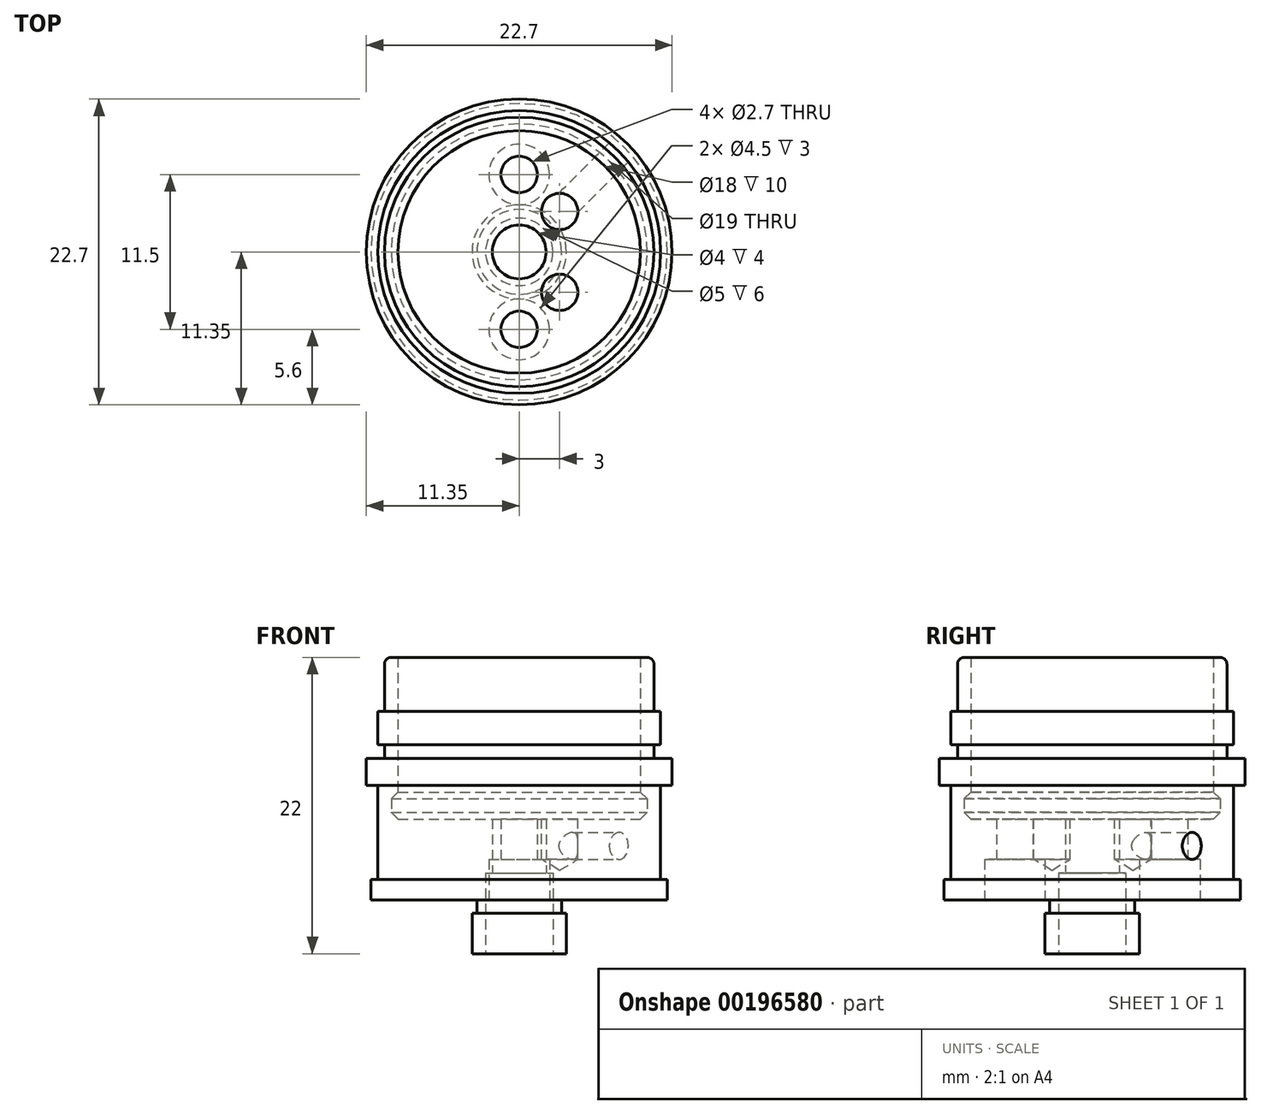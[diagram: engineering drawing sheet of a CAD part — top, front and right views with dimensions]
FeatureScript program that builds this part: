
annotation { "Feature Type Name" : "Feature", "Feature Type Description" : "" }
export const myFeature = defineFeature(function(context is Context, id is Id, definition is map)
    precondition{}
    {
        {
            var Q0;
            Q0=qCreatedBy(makeId("Front.planeOp"),FACE);
            var sketch = newSketch(context, id + "F0", { "sketchPlane" : qUnion([Q0])});
            skLineSegment(sketch, "E0", {"start": v(0, 0) * mm, "end": v(0, 22) * mm, "construction": true});
            skLineSegment(sketch, "E1", {"start": v(9, 22) * mm, "end": v(9.5, 22) * mm});
            skLineSegment(sketch, "E2", {"start": v(10, 21.5) * mm, "end": v(10, 18) * mm});
            skLineSegment(sketch, "E3", {"start": v(10, 18) * mm, "end": v(10.5, 18) * mm});
            skLineSegment(sketch, "E4", {"start": v(10.5, 18) * mm, "end": v(10.5, 15.5) * mm});
            skLineSegment(sketch, "E5", {"start": v(10.5, 15.5) * mm, "end": v(10, 15.5) * mm});
            skLineSegment(sketch, "E6", {"start": v(10, 15.5) * mm, "end": v(10, 14.5) * mm});
            skLineSegment(sketch, "E7", {"start": v(10, 14.5) * mm, "end": v(11.35, 14.5) * mm});
            skLineSegment(sketch, "E8", {"start": v(11.35, 14.5) * mm, "end": v(11.35, 12.5) * mm});
            skLineSegment(sketch, "E9", {"start": v(11.35, 12.5) * mm, "end": v(10.5, 12.5) * mm});
            skLineSegment(sketch, "E10", {"start": v(10.5, 12.5) * mm, "end": v(10.5, 5.5) * mm});
            skLineSegment(sketch, "E11", {"start": v(10.5, 5.5) * mm, "end": v(11, 5.5) * mm});
            skLineSegment(sketch, "E12", {"start": v(9, 22) * mm, "end": v(9, 12) * mm});
            skLineSegment(sketch, "E13", {"start": v(0, 4.88) * mm, "end": v(0, 0) * mm, "construction": true});
            skLineSegment(sketch, "E14", {"start": v(11, 5.5) * mm, "end": v(11, 4) * mm});
            skLineSegment(sketch, "E15", {"start": v(11, 4) * mm, "end": v(3.15, 4) * mm});
            skLineSegment(sketch, "E16", {"start": v(3.15, 4) * mm, "end": v(3.15, 3) * mm});
            skLineSegment(sketch, "E17", {"start": v(3.15, 3) * mm, "end": v(3.5, 3) * mm});
            skLineSegment(sketch, "E18", {"start": v(3.5, 3) * mm, "end": v(3.5, 0) * mm});
            skLineSegment(sketch, "E19", {"start": v(3.5, 0) * mm, "end": v(2.5, 0) * mm});
            skLineSegment(sketch, "E20", {"start": v(2.5, 0) * mm, "end": v(2.5, 6) * mm});
            skLineSegment(sketch, "E21", {"start": v(2.5, 6) * mm, "end": v(2, 6) * mm});
            skLineSegment(sketch, "E22", {"start": v(2, 6) * mm, "end": v(2, 10) * mm});
            skLineSegment(sketch, "E23", {"start": v(9, 10) * mm, "end": v(2, 10) * mm});
            skPoint(sketch, "E24.visualSharp", {"position": v(10, 22) * mm});
            skArc(sketch, "E24.filletArc", {"start": v(10, 21.5) * mm, "mid": v(9.85, 21.85) * mm, "end": v(9.5, 22) * mm});
            skLineSegment(sketch, "E25", {"start": v(9, 12) * mm, "end": v(9.5, 11.5) * mm});
            skLineSegment(sketch, "E26", {"start": v(9.5, 11.5) * mm, "end": v(9.5, 10.5) * mm});
            skLineSegment(sketch, "E27", {"start": v(9, 10) * mm, "end": v(9.5, 10.5) * mm});
            skSolve(sketch);
        }
        {
            var Q0;
            Q0 = qSketchRegion(id + "F0", true);
            var Q1;
            Q1=sQuery(id+"F0.wireOp",EDGE,"E0");
            revolve(context, id + "F1", {"entities" : qUnion([Q0]), "axis" : qUnion([Q1]), "revolveType" : RevolveType.FULL});
        }
        {
            var Q0;
            Q0=makeQuery(id+"F1.opRevolve","SWEPT_FACE",FACE,{"disambiguationData":[OSD([sQuery(id+"F0.wireOp",EDGE,"E15")])]});
            var sketch = newSketch(context, id + "F2", { "sketchPlane" : qUnion([Q0])});
            skPoint(sketch, "E28", {"position": v(0, -5.75) * mm});
            skPoint(sketch, "E29.MirrorP", {"position": v(0, 5.75) * mm});
            skSolve(sketch);
        }
        {
            var Q0;
            Q0=sQuery(id+"F2.wireOp",VERTEX,"E28");
            var Q1;
            Q1=sQuery(id+"F2.wireOp",VERTEX,"E29.MirrorP");
            var Q2;
            Q2=makeQuery(id+"F1.opRevolve","SWEPT_BODY",BODY,{"disambiguationData":[OSD([sQuery(id+"F0.wireOp",EDGE,"E1"),sQuery(id+"F0.wireOp",EDGE,"E2"),sQuery(id+"F0.wireOp",EDGE,"E3"),sQuery(id+"F0.wireOp",EDGE,"E4"),sQuery(id+"F0.wireOp",EDGE,"E5"),sQuery(id+"F0.wireOp",EDGE,"E6"),sQuery(id+"F0.wireOp",EDGE,"E7"),sQuery(id+"F0.wireOp",EDGE,"E8"),sQuery(id+"F0.wireOp",EDGE,"E9"),sQuery(id+"F0.wireOp",EDGE,"E10"),sQuery(id+"F0.wireOp",EDGE,"E11"),sQuery(id+"F0.wireOp",EDGE,"E12"),sQuery(id+"F0.wireOp",EDGE,"E14"),sQuery(id+"F0.wireOp",EDGE,"E15"),sQuery(id+"F0.wireOp",EDGE,"E16"),sQuery(id+"F0.wireOp",EDGE,"E17"),sQuery(id+"F0.wireOp",EDGE,"E18"),sQuery(id+"F0.wireOp",EDGE,"E19"),sQuery(id+"F0.wireOp",EDGE,"E20"),sQuery(id+"F0.wireOp",EDGE,"E21"),sQuery(id+"F0.wireOp",EDGE,"E22"),sQuery(id+"F0.wireOp",EDGE,"E23"),sQuery(id+"F0.wireOp",EDGE,"E24.filletArc"),sQuery(id+"F0.wireOp",EDGE,"E25"),sQuery(id+"F0.wireOp",EDGE,"E26"),sQuery(id+"F0.wireOp",EDGE,"E27")])]});
            hole(context, id + "F3", {"style" : HoleStyle.C_BORE, "endStyle" : HoleEndStyle.THROUGH, "holeDiameter" : 2.7 * mm, "cBoreDiameter" : 4.5 * mm, "cBoreDepth" : 3 * mm, "locations" : qUnion([Q0, Q1]), "scope" : qUnion([Q2]), "isTappedThrough" : true});
        }
        {
            var Q0;
            Q0=makeQuery(id+"F1.opRevolve","SWEPT_FACE",FACE,{"disambiguationData":[OSD([sQuery(id+"F0.wireOp",EDGE,"E23")])]});
            var sketch = newSketch(context, id + "F4", { "sketchPlane" : qUnion([Q0])});
            skPoint(sketch, "E30", {"position": v(3, -3) * mm});
            skPoint(sketch, "E31.MirrorP", {"position": v(3, 3) * mm});
            skSolve(sketch);
        }
        {
            var Q0;
            Q0=sQuery(id+"F4.wireOp",VERTEX,"E30");
            var Q1;
            Q1=sQuery(id+"F4.wireOp",VERTEX,"E31.MirrorP");
            var Q2;
            Q2=makeQuery(id+"F1.opRevolve","SWEPT_BODY",BODY,{"disambiguationData":[OSD([sQuery(id+"F0.wireOp",EDGE,"E1"),sQuery(id+"F0.wireOp",EDGE,"E2"),sQuery(id+"F0.wireOp",EDGE,"E3"),sQuery(id+"F0.wireOp",EDGE,"E4"),sQuery(id+"F0.wireOp",EDGE,"E5"),sQuery(id+"F0.wireOp",EDGE,"E6"),sQuery(id+"F0.wireOp",EDGE,"E7"),sQuery(id+"F0.wireOp",EDGE,"E8"),sQuery(id+"F0.wireOp",EDGE,"E9"),sQuery(id+"F0.wireOp",EDGE,"E10"),sQuery(id+"F0.wireOp",EDGE,"E11"),sQuery(id+"F0.wireOp",EDGE,"E12"),sQuery(id+"F0.wireOp",EDGE,"E14"),sQuery(id+"F0.wireOp",EDGE,"E15"),sQuery(id+"F0.wireOp",EDGE,"E16"),sQuery(id+"F0.wireOp",EDGE,"E17"),sQuery(id+"F0.wireOp",EDGE,"E18"),sQuery(id+"F0.wireOp",EDGE,"E19"),sQuery(id+"F0.wireOp",EDGE,"E20"),sQuery(id+"F0.wireOp",EDGE,"E21"),sQuery(id+"F0.wireOp",EDGE,"E22"),sQuery(id+"F0.wireOp",EDGE,"E23"),sQuery(id+"F0.wireOp",EDGE,"E24.filletArc"),sQuery(id+"F0.wireOp",EDGE,"E25"),sQuery(id+"F0.wireOp",EDGE,"E26"),sQuery(id+"F0.wireOp",EDGE,"E27")])]});
            hole(context, id + "F5", {"style" : HoleStyle.SIMPLE, "endStyle" : HoleEndStyle.BLIND, "holeDiameter" : 2.7 * mm, "holeDepth" : 3 * mm, "locations" : qUnion([Q0, Q1]), "scope" : qUnion([Q2])});
        }
        {
            var Q0;
            Q0=sQuery(id+"F0.wireOp",EDGE,"E0");
            var Q1;
            Q1=sQuery(id+"F4.wireOp",VERTEX,"E31.MirrorP");
            cPlane(context, id + "F6", {"entities" : qUnion([Q0, Q1]), "cplaneType" : CPlaneType.LINE_ANGLE, "offset" : 25 * mm, "angle" : 0 * degree, "width" : 150 * mm, "height" : 150 * mm});
        }
        {
            var Q0;
            Q0=qCreatedBy(id+"F6.planeOp",FACE);
            var sketch = newSketch(context, id + "F7", { "sketchPlane" : qUnion([Q0])});
            skLineSegment(sketch, "E32", {"start": v(-4.24, 8) * mm, "end": v(-16.96, 8) * mm});
            skLineSegment(sketch, "E33", {"start": v(-16.96, 8) * mm, "end": v(-16.96, 9) * mm});
            skLineSegment(sketch, "E34", {"start": v(-16.96, 9) * mm, "end": v(-4.24, 9) * mm});
            skLineSegment(sketch, "E35", {"start": v(-4.24, 9) * mm, "end": v(-4.24, 8) * mm});
            skSolve(sketch);
        }
        {
            var Q0;
            Q0 = qSketchRegion(id + "F7", true);
            var Q1;
            Q1=sQuery(id+"F7.wireOp",EDGE,"E32");
            revolve(context, id + "F8", {"operationType" : NewBodyOperationType.REMOVE, "entities" : qUnion([Q0]), "axis" : qUnion([Q1]), "revolveType" : RevolveType.FULL, "oppositeDirection" : true});
        }
    });
